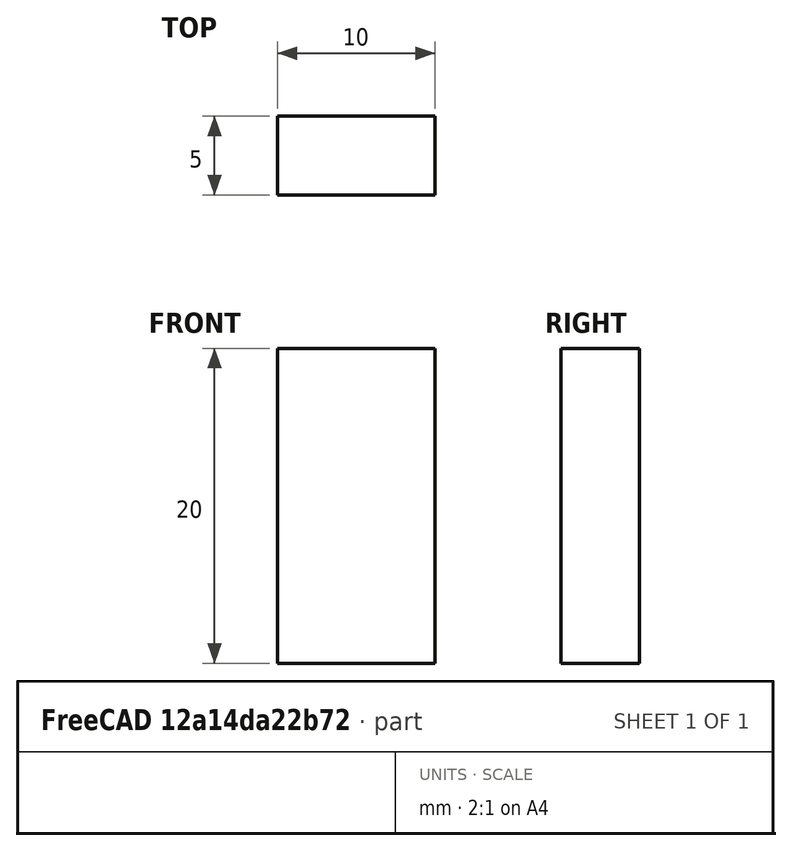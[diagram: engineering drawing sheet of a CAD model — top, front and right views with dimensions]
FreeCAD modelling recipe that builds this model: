
FCSTD DOCUMENT  (FreeCAD 0.17R12595 (Git))
Label: TestCfdFenics
License: All rights reserved
LicenseURL: http://en.wikipedia.org/wiki/All_rights_reserved
objects: Fem::ConstraintFluidBoundary×3, Part::Box×1, App::MeasureDistance×1, Fem::FemSolverObjectPython×1, Fem::FemMeshObjectPython×1, App::MaterialObjectPython×1, Fem::FemAnalysisPython×1
note: 1 computed .brp shape members not serialized (recipe doc carries the construction recipe); baked Part::Feature solids carry a one-line shape summary decoded from their .brp

FEATURE [Part::Box] Box  label="Cube"
  AttacherType = Attacher::AttachEngine3D
  Height = 20
  Length = 10
  Width = 5
FEATURE [Fem::ConstraintFluidBoundary] FluidBoundary  label="Inlet"
  BoundaryType = 0
  BoundaryValue = 0.1
  DirectionVector = (0,0,1)
  HTCoeffValue = 0
  HeatFluxValue = 0
  NormalDirection = (0,0,-1)
  Normals = (9) [(0,0,-1),(0,0,-1),(0,0,-1),(0,0,-1),(0,0,-1),(0,0,-1),(0,0,-1),(0,0,-1),(0,0,-1)]
  Points = (9) [(0,0,0),(5,0,0),(10,0,0),(0,2.5,0),(5,2.5,0),(10,2.5,0),(0,5,0),(5,5,0),(10,5,0)]
  References = -> [Box]
  Reversed = true
  Subtype = 2
  TemperatureValue = 0
  ThermalBoundaryType = 1
  TurbulenceSpecification = 1
  TurbulentIntensityValue = 0
  TurbulentLengthValue = 0
FEATURE [Fem::ConstraintFluidBoundary] FluidBoundary001  label="Outlet"
  BoundaryType = 2
  BoundaryValue = 0
  DirectionVector = (0,0,1)
  HTCoeffValue = 0
  HeatFluxValue = 0
  NormalDirection = (0,0,1)
  Normals = (9) [(0,0,1),(0,0,1),(0,0,1),(0,0,1),(0,0,1),(0,0,1),(0,0,1),(0,0,1),(0,0,1)]
  Points = (9) [(0,0,20),(5,0,20),(10,0,20),(0,2.5,20),(5,2.5,20),(10,2.5,20),(0,5,20),(5,5,20),(10,5,20)]
  References = -> [Box]
  Subtype = 1
  TemperatureValue = 0
  ThermalBoundaryType = 1
  TurbulenceSpecification = 1
  TurbulentIntensityValue = 0
  TurbulentLengthValue = 0
FEATURE [App::MeasureDistance] Distance  label="Distance: 9.74 mm"
  Distance = 9.73591
  P1 = (0,0,0.264091)
  P2 = (0,0,10)
FEATURE [Fem::FemSolverObjectPython] Fenics  # FEM object (typed FeaturePython)
  Buoyant = false
  EndTime = 0
  Gravity = (0,0,0)
  HeatTransfering = false
  InputCaseName = TestCase
  Parallel = false
  PhysicalDomain = 1
  Porous = false
  ResultObtained = true
  StartTime = 0
  TimeStep = 0
  Transient = false
  TurbulenceModel = 0
  WriteInterval = 0
FEATURE [Fem::FemMeshObjectPython] Box_Mesh001  # FEM object (typed FeaturePython)
  Algorithm2D = 3
  Algorithm3D = 3
  CharacteristicLengthMax = 1
  CharacteristicLengthMin = 0
  CoherenceMesh = true
  ElementDimension = 0
  ElementOrder = 0
  GeometryTolerance = 1e-06
  HighOrderOptimize = false
  LengthScalingFactor = 1
  OptimizeNetgen = false
  OptimizeStd = false
  OutputFormat = 0
  Part = -> Box
  RecombineAll = false
FEATURE [App::MaterialObjectPython] FluidMaterial  # material (typed FeaturePython)
  Category = 1
  Material = Density=998.0 kg/m^3,Description=Standard distilled water properties at 20 Degrees Celsius and 1 atm,DynamicViscosity=1.003e-3 kg/m/s,+7 more (map truncated)
FEATURE [Fem::ConstraintFluidBoundary] FluidBoundary002  label="wall"
  BoundaryType = 1
  BoundaryValue = 0
  DirectionVector = (-1,0,0)
  HTCoeffValue = 0
  HeatFluxValue = 0
  NormalDirection = (-1,0,0)
  Normals = (36) [(-1,0,0),(-1,0,0),(-1,0,0),(-1,0,0),(-1,0,0),(-1,0,0),(-1,0,0),(-1,0,0),(-1,0,0),(0,-1,0),(0,-1,0),(0,-1,0),(0,-1,0),(0,-1,0),(0,-1,0),(0,-1,0),+20 more]
  Points = (36) [(0,5,0),(0,5,10),(0,5,20),(0,2.5,0),(0,2.5,10),(0,2.5,20),(0,0,0),(0,0,10),(0,0,20),(0,0,0),(0,0,10),(0,0,20),(5,0,0),(5,0,10),(5,0,20),(10,0,0),+20 more]
  References = -> [Box]
  Subtype = 1
  TemperatureValue = 0
  ThermalBoundaryType = 1
  TurbulenceSpecification = 1
  TurbulentIntensityValue = 0
  TurbulentLengthValue = 0
FEATURE [Fem::FemAnalysisPython] CfdAnalysis  # FEM object (typed FeaturePython)
  Group = -> [FluidBoundary,FluidBoundary001,Fenics,Box_Mesh001,FluidMaterial,FluidBoundary002]
